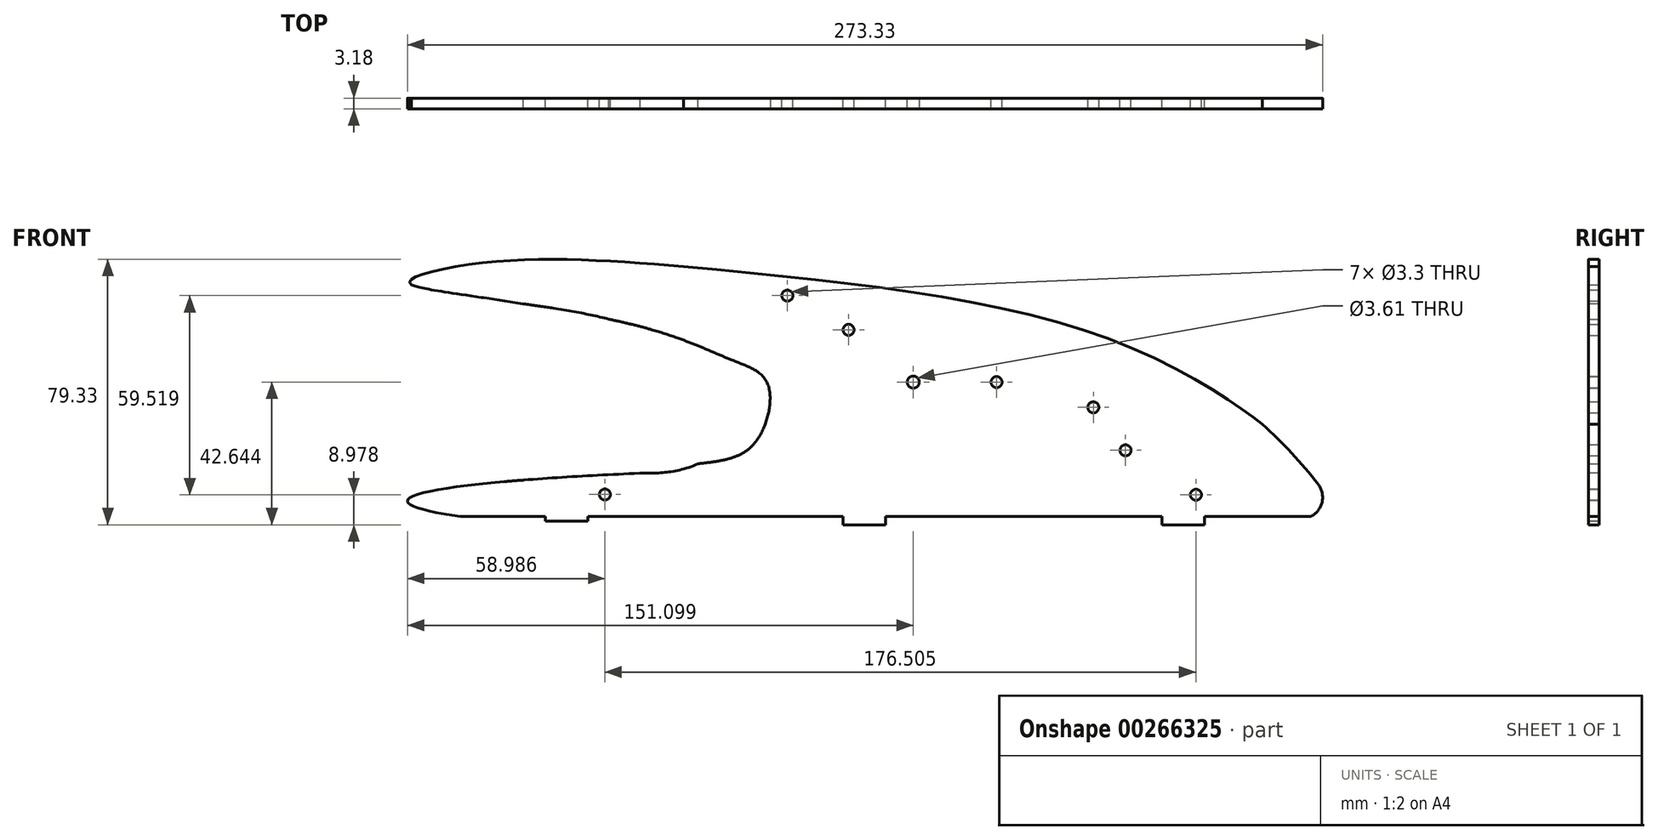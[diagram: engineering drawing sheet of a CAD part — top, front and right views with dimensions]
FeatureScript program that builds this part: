
annotation { "Feature Type Name" : "Feature", "Feature Type Description" : "" }
export const myFeature = defineFeature(function(context is Context, id is Id, definition is map)
    precondition{}
    {
        {
            var Q0;
            Q0=qCreatedBy(makeId("Front.planeOp"),FACE);
            var sketch = newSketch(context, id + "F0", { "sketchPlane" : qUnion([Q0])});
            skCircle(sketch, "E0", {"center": v(-54.6, 31.8) * mm, "radius": 1.65 * mm});
            skCircle(sketch, "E1", {"center": v(-17, 5.94) * mm, "radius": 1.8 * mm});
            skCircle(sketch, "E2", {"center": v(7.87, 5.94) * mm, "radius": 1.65 * mm});
            skPoint(sketch, "E3.bottom.end.orphan", {"position": v(84.7, 23) * mm});
            skPoint(sketch, "E4.orphan", {"position": v(61.55, 23.64) * mm});
            skPoint(sketch, "E5.right.end.orphan", {"position": v(110.1, 23) * mm});
            skPoint(sketch, "E6.visualSharp", {"position": v(22.9, 23.64) * mm});
            skPoint(sketch, "E7.visualSharp", {"position": v(111.38, -35.63) * mm});
            skPoint(sketch, "E6.filletArc.end.orphan", {"position": v(20.95, 23.64) * mm});
            skArc(sketch, "E8", {"start": v(103.94, -24.67) * mm, "mid": v(96.02, -15.26) * mm, "end": v(87.2, -6.68) * mm});
            skPoint(sketch, "E9.centerSnap0", {"position": v(-31.16, 11.37) * mm});
            skPoint(sketch, "E10.trimOffspring.end.orphan", {"position": v(-15.74, 23.64) * mm});
            skPoint(sketch, "E9.center.orphan", {"position": v(-31.16, 23.59) * mm});
            skArc(sketch, "E11.filletArc", {"start": v(101.82, -34.14) * mm, "mid": v(105.08, -29.9) * mm, "end": v(103.94, -24.67) * mm});
            skPoint(sketch, "E12.orphan", {"position": v(-66.42, 22.61) * mm});
            skPoint(sketch, "E13.visualSharp", {"position": v(-66.42, -34.16) * mm});
            skCircle(sketch, "E14", {"center": v(36.77, -1.6) * mm, "radius": 1.65 * mm});
            skPoint(sketch, "E15.visualSharp", {"position": v(-33.01, -34.16) * mm});
            skCircle(sketch, "E16", {"center": v(46.38, -14.43) * mm, "radius": 1.65 * mm});
            skCircle(sketch, "E17", {"center": v(67.4, -27.72) * mm, "radius": 1.65 * mm});
            skCircle(sketch, "E18", {"center": v(-36.34, 21.57) * mm, "radius": 1.65 * mm});
            skFitSpline(sketch, "E19", {"points": [v(-63.32, -34.16) * mm, v(-152.25, -34.16) * mm, v(-168.06, -29.3) * mm, v(-94.32, -21.12) * mm], "startDerivative": vector(-236.09, -7.57) * mm, "endDerivative": vector(279.66, 10.38) * mm});
            skLineSegment(sketch, "E20.trimOffspring", {"start": v(-133.3, -23.31) * mm, "end": v(-133.3, -23.31) * mm});
            skPoint(sketch, "E21.end.orphan", {"position": v(-94.32, 28.47) * mm});
            skPoint(sketch, "E22.visualSharp", {"position": v(-96.66, -21.2) * mm});
            skPoint(sketch, "E23.center.orphan", {"position": v(-17, -34.16) * mm});
            skPoint(sketch, "E24.end.orphan", {"position": v(-17, -23.74) * mm});
            skPoint(sketch, "E25.visualSharp", {"position": v(-38.9, 23.59) * mm});
            skPoint(sketch, "E26.start.orphan", {"position": v(2.6, -34.16) * mm});
            skPoint(sketch, "E27.trimOffspring.end.orphan", {"position": v(157.22, 0) * mm});
            skCircle(sketch, "E28", {"center": v(-109.11, -27.65) * mm, "radius": 1.65 * mm});
            skFitSpline(sketch, "E29", {"points": [v(-83.78, 15.71) * mm, v(-63.34, 0) * mm, v(-81.24, -18.44) * mm, v(-98.75, -21.3) * mm], "startDerivative": vector(86.1, -39.19) * mm, "endDerivative": vector(-54.02, -0.6) * mm});
            skFitSpline(sketch, "E30.trimOffspring", {"points": [v(-104.02, 23.59) * mm, v(-63.34, 0) * mm, v(-96.64, -21.54) * mm], "startDerivative": vector(116.52, -45.31) * mm, "endDerivative": vector(-104.9, -44.93) * mm});
            skFitSpline(sketch, "E31", {"points": [v(-133.3, -23.31) * mm, v(-81.24, -18.44) * mm, v(-65.9, -13.83) * mm, v(-60.08, -2.32) * mm, v(-61.56, 7.26) * mm, v(-71.48, 12.67) * mm, v(-98.75, 22.61) * mm, v(-160.36, 33.45) * mm, v(-167.38, 35.25) * mm], "startDerivative": vector(304.25, 34.53) * mm, "endDerivative": vector(-59.04, 28.98) * mm});
            skFitSpline(sketch, "E32.trimOffspring", {"points": [v(-88.26, 10.54) * mm, v(-104.02, 23.59) * mm, v(-167.22, 35.31) * mm, v(-146, 41.55) * mm, v(-85.65, 40.52) * mm], "startDerivative": vector(-45.67, 79.49) * mm, "endDerivative": vector(197.72, -15.64) * mm});
            skPoint(sketch, "E33.1.internal.orphan", {"position": v(-104.44, 22.61) * mm});
            skPoint(sketch, "E33.3.internal.orphan", {"position": v(-152.25, 40.96) * mm});
            skFitSpline(sketch, "E34", {"points": [v(-85.65, 40.52) * mm, v(41.45, 18.88) * mm, v(87.2, -6.68) * mm, v(92.36, -11.49) * mm], "startDerivative": vector(260.67, -24.77) * mm, "endDerivative": vector(30.28, -32.67) * mm});
            skPoint(sketch, "E35.end.orphan", {"position": v(2.6, 23.64) * mm});
            skLineSegment(sketch, "E36", {"start": v(-160.23, 33.1) * mm, "end": v(-139.25, -23.82) * mm});
            skLineSegment(sketch, "E37", {"start": v(-153.03, 31.95) * mm, "end": v(-132.7, -23.24) * mm});
            skLineSegment(sketch, "E38", {"start": v(-146.01, 31.26) * mm, "end": v(-126.2, -22.47) * mm});
            skLineSegment(sketch, "E39", {"start": v(-138.8, 30.05) * mm, "end": v(-119.65, -21.9) * mm});
            skPoint(sketch, "E40.orphan", {"position": v(-139.25, 31.26) * mm});
            skLineSegment(sketch, "E41", {"start": v(-126.2, -22.47) * mm, "end": v(-126.18, -22.54) * mm});
            skLineSegment(sketch, "E42", {"start": v(-113.1, -21.3) * mm, "end": v(-131.68, 29.1) * mm});
            skLineSegment(sketch, "E43", {"start": v(-124.52, 28.04) * mm, "end": v(-106.55, -20.72) * mm});
            skLineSegment(sketch, "E44", {"start": v(-117.22, 26.58) * mm, "end": v(-99.99, -20.16) * mm});
            skLineSegment(sketch, "E45", {"start": v(-93.43, -19.6) * mm, "end": v(-109.93, 25.17) * mm});
            skLineSegment(sketch, "E46", {"start": v(-102.57, 23.56) * mm, "end": v(-86.88, -19.01) * mm});
            skLineSegment(sketch, "E47", {"start": v(-80.35, -18.34) * mm, "end": v(-95.08, 21.61) * mm});
            skLineSegment(sketch, "E48", {"start": v(-87.4, 19.14) * mm, "end": v(-73.94, -17.4) * mm});
            skLineSegment(sketch, "E49", {"start": v(-79.5, 16.06) * mm, "end": v(-67.94, -15.3) * mm});
            skLineSegment(sketch, "E50", {"start": v(-71.48, 12.67) * mm, "end": v(-63, -10.32) * mm});
            skFitSpline(sketch, "E51.trimOffspring", {"points": [v(-88.26, 10.54) * mm, v(-104.02, 23.59) * mm, v(-167.22, 35.31) * mm, v(-146, 41.55) * mm, v(-85.65, 40.52) * mm], "startDerivative": vector(-45.67, 79.49) * mm, "endDerivative": vector(197.72, -15.64) * mm});
            skLineSegment(sketch, "E52", {"start": v(-63.34, 8.92) * mm, "end": v(-59.84, -0.55) * mm});
            skPoint(sketch, "E53.newPointB", {"position": v(116.49, -34.16) * mm});
            skArc(sketch, "E53.filletArc", {"start": v(101.76, -34.16) * mm, "mid": v(101.8, -34.15) * mm, "end": v(101.82, -34.14) * mm});
            skPoint(sketch, "E54.end.orphan", {"position": v(58.44, -34.16) * mm});
            skPoint(sketch, "E3.top.end.orphan", {"position": v(78.52, -34.16) * mm});
            skLineSegment(sketch, "E55", {"start": v(101.76, -34.16) * mm, "end": v(70, -34.16) * mm});
            skArc(sketch, "E56.filletArc", {"start": v(-152.26, -34.15) * mm, "mid": v(-152.25, -34.16) * mm, "end": v(-152.24, -34.16) * mm});
            skLineSegment(sketch, "E57.trimOffspring", {"start": v(-57.48, -34.16) * mm, "end": v(-114.15, -34.16) * mm});
            skLineSegment(sketch, "E58.trimOffspring", {"start": v(57.3, -34.16) * mm, "end": v(-25.25, -34.16) * mm});
            skLineSegment(sketch, "E59.trimOffspring", {"start": v(-126.85, -34.16) * mm, "end": v(-152.24, -34.16) * mm});
            skLineSegment(sketch, "E60", {"start": v(-57.48, -34.16) * mm, "end": v(-37.95, -34.16) * mm});
            skPoint(sketch, "E61.start.orphan", {"position": v(-57.48, -31.62) * mm});
            skLineSegment(sketch, "E62.top", {"start": v(-37.95, -36.7) * mm, "end": v(-25.25, -36.7) * mm});
            skLineSegment(sketch, "E62.left", {"start": v(-37.95, -34.16) * mm, "end": v(-37.95, -36.7) * mm});
            skLineSegment(sketch, "E62.right", {"start": v(-25.25, -34.16) * mm, "end": v(-25.25, -36.7) * mm});
            skPoint(sketch, "E63.start.orphan", {"position": v(-44.78, -31.62) * mm});
            skPoint(sketch, "E64.start.orphan", {"position": v(-32.08, -31.62) * mm});
            skLineSegment(sketch, "E65", {"start": v(-25.25, -34.16) * mm, "end": v(-25.25, -34.16) * mm});
            skPoint(sketch, "E66.end.orphan", {"position": v(-76, -21.12) * mm});
            skPoint(sketch, "E67.trimOffspring.2.internal.orphan", {"position": v(-117.22, 35.25) * mm});
            skLineSegment(sketch, "E68.top", {"start": v(57.3, -36.7) * mm, "end": v(70, -36.7) * mm});
            skLineSegment(sketch, "E68.left", {"start": v(57.3, -34.16) * mm, "end": v(57.3, -36.7) * mm});
            skLineSegment(sketch, "E68.right", {"start": v(70, -34.16) * mm, "end": v(70, -36.7) * mm});
            skPoint(sketch, "E69.end.orphan", {"position": v(61.87, -31.62) * mm});
            skPoint(sketch, "E70.start.orphan", {"position": v(49.17, -31.62) * mm});
            skPoint(sketch, "E71.start.orphan", {"position": v(-127.45, -31.62) * mm});
            skPoint(sketch, "E72.start.orphan", {"position": v(-114.75, -31.62) * mm});
            skLineSegment(sketch, "E73.top", {"start": v(-126.85, -36.7) * mm, "end": v(-114.15, -36.7) * mm});
            skLineSegment(sketch, "E73.left", {"start": v(-126.85, -34.16) * mm, "end": v(-126.85, -36.7) * mm});
            skLineSegment(sketch, "E73.right", {"start": v(-114.15, -34.16) * mm, "end": v(-114.15, -36.7) * mm});
            skSolve(sketch);
        }
        {
            var Q0;
            Q0=makeQuery(id+"F0.imprint","IMPRINT",FACE,{"disambiguationData":[TD([[makeQuery(id+"F0.imprint","IMPRINT",EDGE,{"derivedFrom":sQuery(id+"F0.wireOp",EDGE,"lP6l2hqg-zXf5-B6bm-zcnX-EUkdIj4Gj8fv.top")}),1.0]])]});
            var Q1;
            Q1=makeQuery(id+"F0.imprint","IMPRINT",FACE,{"disambiguationData":[TD([[makeQuery(id+"F0.imprint","IMPRINT",EDGE,{"derivedFrom":sQuery(id+"F0.wireOp",EDGE,"E0")}),-1.0]])]});
            extrude(context, id + "F1", {"entities" : qUnion([Q0, Q1]), "depth" : 3.17 * mm, "offsetDistance" : 25.4 * mm});
        }
    });
